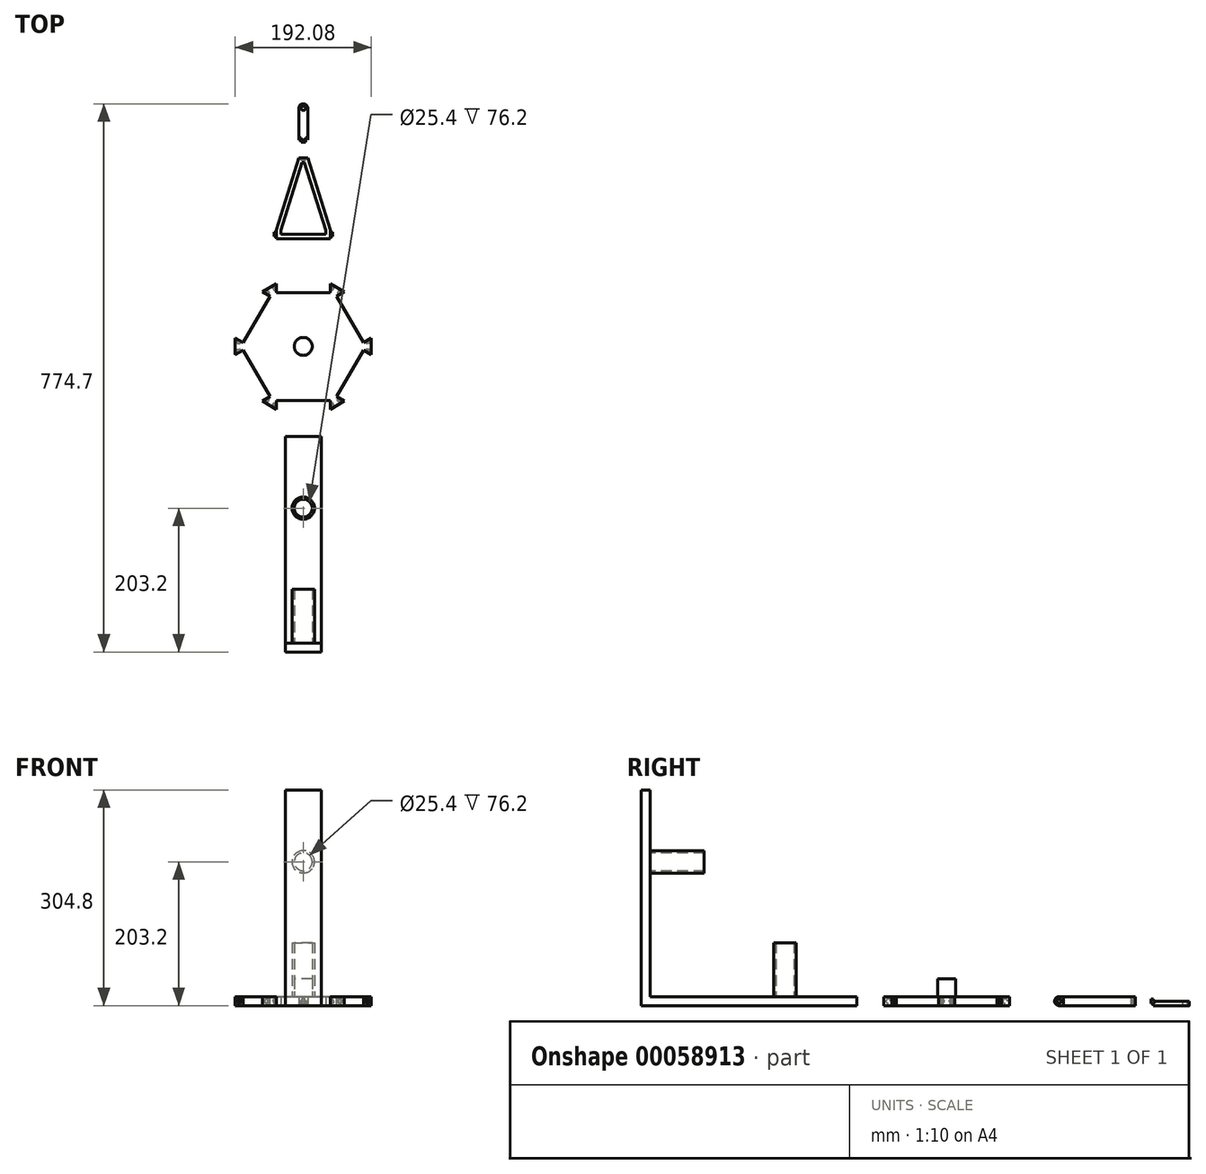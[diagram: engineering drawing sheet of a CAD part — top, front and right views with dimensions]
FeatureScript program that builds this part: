
annotation { "Feature Type Name" : "Feature", "Feature Type Description" : "" }
export const myFeature = defineFeature(function(context is Context, id is Id, definition is map)
    precondition{}
    {
        {
            var Q0;
            Q0=qCreatedBy(makeId("Top.planeOp"),FACE);
            var sketch = newSketch(context, id + "F0", { "sketchPlane" : qUnion([Q0])});
            skCircle(sketch, "E0.cCircle", {"center": v(0, 0) * mm, "radius": 76.2 * mm, "construction": true});
            skLineSegment(sketch, "E0.0", {"start": v(-44, 76.2) * mm, "end": v(44, 76.2) * mm});
            skLineSegment(sketch, "E0.1", {"start": v(44, 76.2) * mm, "end": v(87.99, 0) * mm});
            skLineSegment(sketch, "E0.2", {"start": v(87.99, 0) * mm, "end": v(44, -76.2) * mm});
            skLineSegment(sketch, "E0.3", {"start": v(44, -76.2) * mm, "end": v(-44, -76.2) * mm});
            skLineSegment(sketch, "E0.4", {"start": v(-44, -76.2) * mm, "end": v(-87.99, 0) * mm});
            skLineSegment(sketch, "E0.5", {"start": v(-87.99, 0) * mm, "end": v(-44, 76.2) * mm});
            skPoint(sketch, "E0.0.midPoint", {"position": v(0, 76.2) * mm});
            skSolve(sketch);
        }
        {
            var Q0;
            Q0=makeQuery(id+"F0.imprint","IMPRINT",FACE,{"disambiguationData":[TD([[makeQuery(id+"F0.imprint","IMPRINT",EDGE,{"derivedFrom":sQuery(id+"F0.wireOp",EDGE,"E0.0")}),-1.0]])]});
            extrude(context, id + "F1", {"entities" : qUnion([Q0]), "depth" : 12.7 * mm});
        }
        {
            var Q0;
            Q0=makeQuery(id+"F1.opExtrude","CAP_FACE",FACE,{"disambiguationData":[OSD([sQuery(id+"F0.wireOp",EDGE,"E0.0"),sQuery(id+"F0.wireOp",EDGE,"E0.1"),sQuery(id+"F0.wireOp",EDGE,"E0.2"),sQuery(id+"F0.wireOp",EDGE,"E0.3"),sQuery(id+"F0.wireOp",EDGE,"E0.4"),sQuery(id+"F0.wireOp",EDGE,"E0.5")])],"isStart":false});
            var sketch = newSketch(context, id + "F2", { "sketchPlane" : qUnion([Q0])});
            skLineSegment(sketch, "E1", {"start": v(-85.04, 5.1) * mm, "end": v(-96.04, 11.45) * mm});
            skLineSegment(sketch, "E2", {"start": v(-96.04, 11.45) * mm, "end": v(-96.04, -11.45) * mm});
            skLineSegment(sketch, "E3", {"start": v(-96.04, -11.45) * mm, "end": v(-85.04, -5.1) * mm});
            skLineSegment(sketch, "E4", {"start": v(-120.82, 0) * mm, "end": v(103.85, 0) * mm, "construction": true});
            skLineSegment(sketch, "E5", {"start": v(-85.04, 5.1) * mm, "end": v(-85.04, -5.1) * mm});
            skLineSegment(sketch, "E6", {"start": v(0, 0) * mm, "end": v(-66, 38.1) * mm, "construction": true});
            skSolve(sketch);
        }
        {
            var Q0;
            {var subQ5=sQuery(id+"F2.wireOp",EDGE,"E1");Q0=makeQuery(id+"F2.imprint","IMPRINT",FACE,{"disambiguationData":[TD([[makeQuery(id+"F2.imprint","IMPRINT",EDGE,{"derivedFrom":subQ5}),1.0]])]});}
            var Q1;
            Q1=makeQuery(id+"F1.opExtrude","CAP_FACE",FACE,{"disambiguationData":[OSD([sQuery(id+"F0.wireOp",EDGE,"E0.0"),sQuery(id+"F0.wireOp",EDGE,"E0.1"),sQuery(id+"F0.wireOp",EDGE,"E0.2"),sQuery(id+"F0.wireOp",EDGE,"E0.3"),sQuery(id+"F0.wireOp",EDGE,"E0.4"),sQuery(id+"F0.wireOp",EDGE,"E0.5")])],"isStart":true});
            extrude(context, id + "F3", {"entities" : qUnion([Q0]), "operationType" : NewBodyOperationType.ADD, "endBound" : BoundingType.UP_TO_SURFACE, "oppositeDirection" : true, "endBoundEntityFace" : qUnion([Q1]), "depth" : 25.4 * mm});
        }
        {
            var Q0;
            Q0=makeQuery(id+"F3.opExtrude","SWEPT_FACE",FACE,{"disambiguationData":[OSD([sQuery(id+"F2.wireOp",EDGE,"E3")])]});
            var sketch = newSketch(context, id + "F4", { "sketchPlane" : qUnion([Q0])});
            skPoint(sketch, "E7", {"position": v(-82.55, 6.35) * mm});
            skLineSegment(sketch, "E8", {"start": v(-88.9, 12.7) * mm, "end": v(-76.2, 0) * mm});
            skSolve(sketch);
        }
        {
            var Q0;
            Q0=sQuery(id+"F4.wireOp",VERTEX,"E7");
            var Q1;
            Q1=makeQuery(id+"F1.opExtrude","SWEPT_BODY",BODY,{"disambiguationData":[OSD([sQuery(id+"F0.wireOp",EDGE,"E0.0"),sQuery(id+"F0.wireOp",EDGE,"E0.1"),sQuery(id+"F0.wireOp",EDGE,"E0.2"),sQuery(id+"F0.wireOp",EDGE,"E0.3"),sQuery(id+"F0.wireOp",EDGE,"E0.4"),sQuery(id+"F0.wireOp",EDGE,"E0.5")])]});
            hole(context, id + "F5", {"style" : HoleStyle.SIMPLE, "holeDiameter" : 6.35 * mm, "endStyle" : HoleEndStyle.BLIND, "holeDepth" : 3.17 * mm, "locations" : qUnion([Q0]), "scope" : qUnion([Q1])});
        }
        {
            var Q0;
            Q0=makeQuery(id+"F3.opExtrude","SWEPT_FACE",FACE,{"disambiguationData":[OSD([sQuery(id+"F2.wireOp",EDGE,"E1")])]});
            var sketch = newSketch(context, id + "F6", { "sketchPlane" : qUnion([Q0])});
            skLineSegment(sketch, "E9", {"start": v(76.2, 12.7) * mm, "end": v(88.9, 0) * mm, "construction": true});
            skPoint(sketch, "E10", {"position": v(82.55, 6.35) * mm});
            skSolve(sketch);
        }
        {
            var Q0;
            Q0=sQuery(id+"F6.wireOp",VERTEX,"E10");
            var Q1;
            Q1=makeQuery(id+"F1.opExtrude","SWEPT_BODY",BODY,{"disambiguationData":[OSD([sQuery(id+"F0.wireOp",EDGE,"E0.0"),sQuery(id+"F0.wireOp",EDGE,"E0.1"),sQuery(id+"F0.wireOp",EDGE,"E0.2"),sQuery(id+"F0.wireOp",EDGE,"E0.3"),sQuery(id+"F0.wireOp",EDGE,"E0.4"),sQuery(id+"F0.wireOp",EDGE,"E0.5")])]});
            hole(context, id + "F7", {"style" : HoleStyle.SIMPLE, "holeDiameter" : 6.35 * mm, "endStyle" : HoleEndStyle.BLIND, "holeDepth" : 3.17 * mm, "locations" : qUnion([Q0]), "scope" : qUnion([Q1])});
        }
        {
            var Q0;
            {var subQ0=sQuery(id+"F0.wireOp",EDGE,"E0.5");var subQ1=sQuery(id+"F0.wireOp",EDGE,"E0.4");Q0=makeQuery(id+"F3.boolean.opBoolean","MERGE",FACE,{"derivedFrom":[makeQuery(id+"F1.opExtrude","CAP_FACE",FACE,{"disambiguationData":[OSD([sQuery(id+"F0.wireOp",EDGE,"E0.0"),sQuery(id+"F0.wireOp",EDGE,"E0.1"),sQuery(id+"F0.wireOp",EDGE,"E0.2"),sQuery(id+"F0.wireOp",EDGE,"E0.3"),subQ1,subQ0])],"isStart":false}),makeQuery(id+"F3.opExtrude","CAP_FACE",FACE,{"disambiguationData":[OSD([subQ1,subQ0,sQuery(id+"F2.wireOp",EDGE,"E1"),sQuery(id+"F2.wireOp",EDGE,"E2"),sQuery(id+"F2.wireOp",EDGE,"E3")])],"isStart":true})]});}
            var sketch = newSketch(context, id + "F8", { "sketchPlane" : qUnion([Q0])});
            skCircle(sketch, "E11", {"center": v(0, 0) * mm, "radius": 12.7 * mm});
            skSolve(sketch);
        }
        {
            var Q0;
            Q0 = qSketchRegion(id + "F8", true);
            extrude(context, id + "F9", {"entities" : qUnion([Q0]), "operationType" : NewBodyOperationType.ADD, "depth" : 25.4 * mm});
        }
        {
            var Q0;
            Q0=makeQuery(id+"F1.opExtrude","SWEPT_BODY",BODY,{"disambiguationData":[OSD([sQuery(id+"F0.wireOp",EDGE,"E0.0"),sQuery(id+"F0.wireOp",EDGE,"E0.1"),sQuery(id+"F0.wireOp",EDGE,"E0.2"),sQuery(id+"F0.wireOp",EDGE,"E0.3"),sQuery(id+"F0.wireOp",EDGE,"E0.4"),sQuery(id+"F0.wireOp",EDGE,"E0.5")])]});
            var Q1;
            Q1=makeQuery(id+"F9.opExtrude","SWEPT_FACE",FACE,{"disambiguationData":[OSD([sQuery(id+"F8.wireOp",EDGE,"E11")])]});
            circularPattern(context, id + "F10", {"operationType" : NewBodyOperationType.ADD, "entities" : qUnion([Q0]), "axis" : qUnion([Q1]), "angle" : 60 * degree, "instanceCount" : 6});
        }
        {
            var Q0;
            Q0=qCreatedBy(makeId("Top.planeOp"),FACE);
            var sketch = newSketch(context, id + "F11", { "sketchPlane" : qUnion([Q0])});
            skLineSegment(sketch, "E12", {"start": v(-38.1, 152.4) * mm, "end": v(38.1, 152.4) * mm});
            skLineSegment(sketch, "E13", {"start": v(38.1, 152.4) * mm, "end": v(38.1, 165.1) * mm});
            skLineSegment(sketch, "E14", {"start": v(38.1, 165.1) * mm, "end": v(6.35, 266.7) * mm});
            skLineSegment(sketch, "E15", {"start": v(6.35, 266.7) * mm, "end": v(-6.35, 266.7) * mm});
            skLineSegment(sketch, "E16", {"start": v(-6.35, 266.7) * mm, "end": v(-38.1, 165.1) * mm});
            skLineSegment(sketch, "E17", {"start": v(-38.1, 165.1) * mm, "end": v(-38.1, 152.4) * mm});
            skLineSegment(sketch, "E18", {"start": v(0, 266.7) * mm, "end": v(0, 152.4) * mm, "construction": true});
            skLineSegment(sketch, "E19.0", {"start": v(1.68, 260.35) * mm, "end": v(-1.68, 260.35) * mm});
            skLineSegment(sketch, "E19.1", {"start": v(-31.75, 164.13) * mm, "end": v(-31.75, 158.75) * mm});
            skLineSegment(sketch, "E19.2", {"start": v(-31.75, 158.75) * mm, "end": v(31.75, 158.75) * mm});
            skLineSegment(sketch, "E19.3", {"start": v(-1.68, 260.35) * mm, "end": v(-31.75, 164.13) * mm});
            skLineSegment(sketch, "E19.4", {"start": v(31.75, 158.75) * mm, "end": v(31.75, 164.13) * mm});
            skLineSegment(sketch, "E19.5", {"start": v(31.75, 164.13) * mm, "end": v(1.68, 260.35) * mm});
            skSolve(sketch);
        }
        {
            var Q0;
            Q0=makeQuery(id+"F11.imprint","IMPRINT",FACE,{"disambiguationData":[TD([[makeQuery(id+"F11.imprint","IMPRINT",EDGE,{"derivedFrom":sQuery(id+"F11.wireOp",EDGE,"E12")}),1.0]])]});
            extrude(context, id + "F12", {"entities" : qUnion([Q0]), "depth" : 12.7 * mm});
        }
        {
            var Q0;
            Q0=makeQuery(id+"F12.opExtrude","CAP_EDGE",EDGE,{"disambiguationData":[OSD([sQuery(id+"F11.wireOp",EDGE,"E12")])],"isStart":false});
            var Q1;
            Q1=makeQuery(id+"F12.opExtrude","CAP_EDGE",EDGE,{"disambiguationData":[OSD([sQuery(id+"F11.wireOp",EDGE,"E12")])],"isStart":true});
            fillet(context, id + "F13", {"entities" : qUnion([Q0, Q1]), "radius" : 6.35 * mm, "tangentPropagation" : true, "allowEdgeOverflow" : false});
        }
        {
            var Q0;
            Q0=makeQuery(id+"F12.opExtrude","SWEPT_FACE",FACE,{"disambiguationData":[OSD([sQuery(id+"F11.wireOp",EDGE,"E13")])]});
            var sketch = newSketch(context, id + "F14", { "sketchPlane" : qUnion([Q0])});
            skCircle(sketch, "E20", {"center": v(158.75, 6.35) * mm, "radius": 3.18 * mm});
            skSolve(sketch);
        }
        {
            var Q0;
            Q0=makeQuery(id+"F14.imprint","IMPRINT",FACE,{"disambiguationData":[TD([[makeQuery(id+"F14.imprint","IMPRINT",EDGE,{"derivedFrom":sQuery(id+"F14.wireOp",EDGE,"E20")}),1.0]])]});
            extrude(context, id + "F15", {"entities" : qUnion([Q0]), "operationType" : NewBodyOperationType.ADD, "depth" : 3.17 * mm});
        }
        {
            var Q0;
            Q0=makeQuery(id+"F15.opExtrude","SWEPT_FACE",FACE,{"disambiguationData":[OSD([sQuery(id+"F14.wireOp",EDGE,"E20")])]});
            var Q1;
            Q1=makeQuery(id+"F15.opExtrude","CAP_FACE",FACE,{"disambiguationData":[OSD([sQuery(id+"F14.wireOp",EDGE,"E20")])],"isStart":false});
            var Q2;
            Q2=qCreatedBy(makeId("Right.planeOp"),FACE);
            mirror(context, id + "F16", {"faces" : qUnion([Q0, Q1]), "mirrorPlane" : qUnion([Q2]), "patternType" : MirrorType.FACE});
        }
        {
            var Q0;
            Q0=makeQuery(id+"F12.opExtrude","SWEPT_FACE",FACE,{"disambiguationData":[OSD([sQuery(id+"F11.wireOp",EDGE,"E15")])]});
            var sketch = newSketch(context, id + "F17", { "sketchPlane" : qUnion([Q0])});
            skLineSegment(sketch, "E21", {"start": v(-6.35, 12.7) * mm, "end": v(6.35, 0) * mm, "construction": true});
            skPoint(sketch, "E22", {"position": v(0, 6.35) * mm});
            skSolve(sketch);
        }
        {
            var Q0;
            Q0=sQuery(id+"F17.wireOp",VERTEX,"E22");
            var Q1;
            Q1=makeQuery(id+"F12.opExtrude","SWEPT_BODY",BODY,{"disambiguationData":[OSD([sQuery(id+"F11.wireOp",EDGE,"E12"),sQuery(id+"F11.wireOp",EDGE,"E13"),sQuery(id+"F11.wireOp",EDGE,"E14"),sQuery(id+"F11.wireOp",EDGE,"E15"),sQuery(id+"F11.wireOp",EDGE,"E16"),sQuery(id+"F11.wireOp",EDGE,"E17"),sQuery(id+"F11.wireOp",EDGE,"E19.0"),sQuery(id+"F11.wireOp",EDGE,"E19.1"),sQuery(id+"F11.wireOp",EDGE,"E19.2"),sQuery(id+"F11.wireOp",EDGE,"E19.3"),sQuery(id+"F11.wireOp",EDGE,"E19.4"),sQuery(id+"F11.wireOp",EDGE,"E19.5")])]});
            hole(context, id + "F18", {"style" : HoleStyle.SIMPLE, "holeDiameter" : 6.35 * mm, "endStyle" : HoleEndStyle.BLIND, "holeDepth" : 3.17 * mm, "locations" : qUnion([Q0]), "scope" : qUnion([Q1])});
        }
        {
            var Q0;
            Q0=qCreatedBy(makeId("Top.planeOp"),FACE);
            var sketch = newSketch(context, id + "F19", { "sketchPlane" : qUnion([Q0])});
            skLineSegment(sketch, "E23.rect.bottom", {"start": v(6.35, 292.1) * mm, "end": v(-6.35, 292.1) * mm});
            skLineSegment(sketch, "E23.rect.top", {"start": v(6.35, 342.9) * mm, "end": v(-6.35, 342.9) * mm});
            skLineSegment(sketch, "E23.rect.left", {"start": v(6.35, 292.1) * mm, "end": v(6.35, 342.9) * mm});
            skLineSegment(sketch, "E23.rect.right", {"start": v(-6.35, 292.1) * mm, "end": v(-6.35, 342.9) * mm});
            skPoint(sketch, "E23.rect.middle", {"position": v(0, 317.5) * mm});
            skCircle(sketch, "E24", {"center": v(0, 336.55) * mm, "radius": 3.18 * mm});
            skSolve(sketch);
        }
        {
            var Q0;
            Q0=makeQuery(id+"F19.imprint","IMPRINT",FACE,{"disambiguationData":[TD([[makeQuery(id+"F19.imprint","IMPRINT",EDGE,{"derivedFrom":sQuery(id+"F19.wireOp",EDGE,"E23.rect.bottom")}),-1.0]])]});
            extrude(context, id + "F20", {"entities" : qUnion([Q0]), "depth" : 6.35 * mm});
        }
        {
            var Q0;
            Q0=makeQuery(id+"F20.opExtrude","SWEPT_EDGE",EDGE,{"disambiguationData":[OSD([sQuery(id+"F19.wireOp",EDGE,"E23.rect.top"),sQuery(id+"F19.wireOp",EDGE,"E23.rect.right")])]});
            var Q1;
            Q1=makeQuery(id+"F20.opExtrude","SWEPT_EDGE",EDGE,{"disambiguationData":[OSD([sQuery(id+"F19.wireOp",EDGE,"E23.rect.top"),sQuery(id+"F19.wireOp",EDGE,"E23.rect.left")])]});
            fillet(context, id + "F21", {"entities" : qUnion([Q0, Q1]), "radius" : 6.35 * mm, "tangentPropagation" : true, "allowEdgeOverflow" : false});
        }
        {
            var Q0;
            Q0=makeQuery(id+"F20.opExtrude","SWEPT_FACE",FACE,{"disambiguationData":[OSD([sQuery(id+"F19.wireOp",EDGE,"E23.rect.bottom")])]});
            var sketch = newSketch(context, id + "F22", { "sketchPlane" : qUnion([Q0])});
            skCircle(sketch, "E25", {"center": v(0, 6.35) * mm, "radius": 3.18 * mm});
            skSolve(sketch);
        }
        {
            var Q0;
            {var subQ0=sQuery(id+"F22.wireOp",EDGE,"E25");var subQ1=makeQuery(id+"F20.opExtrude","CAP_EDGE",EDGE,{"disambiguationData":[OSD([sQuery(id+"F19.wireOp",EDGE,"E23.rect.bottom")])],"isStart":false});var subQ2=makeQuery(id+"F22.imprint","INTERSECT",VERTEX,{"disambiguationData":[OD(0.0)],"derivedFrom":[subQ1,subQ0]});Q0=makeQuery(id+"F22.imprint","IMPRINT",FACE,{"disambiguationData":[TD([[makeQuery(id+"F22.imprint","IMPRINT",EDGE,{"disambiguationData":[TD([[subQ2,1.0]])],"derivedFrom":subQ0}),1.0]])]});}
            var Q1;
            {var subQ0=sQuery(id+"F22.wireOp",EDGE,"E25");var subQ1=makeQuery(id+"F20.opExtrude","CAP_EDGE",EDGE,{"disambiguationData":[OSD([sQuery(id+"F19.wireOp",EDGE,"E23.rect.bottom")])],"isStart":false});var subQ2=makeQuery(id+"F22.imprint","INTERSECT",VERTEX,{"disambiguationData":[OD(0.0)],"derivedFrom":[subQ1,subQ0]});Q1=makeQuery(id+"F22.imprint","IMPRINT",FACE,{"disambiguationData":[TD([[makeQuery(id+"F22.imprint","IMPRINT",EDGE,{"disambiguationData":[TD([[subQ2,-1.0]])],"derivedFrom":subQ0}),1.0]])]});}
            extrude(context, id + "F23", {"entities" : qUnion([Q0, Q1]), "operationType" : NewBodyOperationType.ADD, "depth" : 3.17 * mm});
        }
        {
            var Q0;
            {var subQ0=sQuery(id+"F19.wireOp",EDGE,"E23.rect.bottom");Q0=makeQuery(id+"F23.boolean.opBoolean","SPLIT",EDGE,{"disambiguationData":[topologyDisambiguationEdgeConnected([makeQuery(id+"F20.opExtrude","CAP_FACE",FACE,{"disambiguationData":[OSD([subQ0,sQuery(id+"F19.wireOp",EDGE,"E23.rect.top"),sQuery(id+"F19.wireOp",EDGE,"E23.rect.left"),sQuery(id+"F19.wireOp",EDGE,"E23.rect.right"),sQuery(id+"F19.wireOp",EDGE,"E24")])],"isStart":false}),makeQuery(id+"F23.opExtrude","CAP_FACE",FACE,{"disambiguationData":[OSD([sQuery(id+"F22.wireOp",EDGE,"E25")])],"isStart":true})])],"derivedFrom":makeQuery(id+"F20.opExtrude","CAP_EDGE",EDGE,{"disambiguationData":[OSD([subQ0])],"isStart":false})});}
            chamfer(context, id + "F24", {"entities" : qUnion([Q0]), "width" : 3.17 * mm, "tangentPropagation" : true});
        }
        {
            var Q0;
            Q0=qCreatedBy(makeId("Right.planeOp"),FACE);
            var sketch = newSketch(context, id + "F25", { "sketchPlane" : qUnion([Q0])});
            skLineSegment(sketch, "E26", {"start": v(-127, 0) * mm, "end": v(-127, 12.7) * mm});
            skLineSegment(sketch, "E27", {"start": v(-127, 12.7) * mm, "end": v(-419.1, 12.7) * mm});
            skLineSegment(sketch, "E28", {"start": v(-419.1, 12.7) * mm, "end": v(-419.1, 304.8) * mm});
            skLineSegment(sketch, "E29", {"start": v(-419.1, 304.8) * mm, "end": v(-431.8, 304.8) * mm});
            skLineSegment(sketch, "E30", {"start": v(-431.8, 304.8) * mm, "end": v(-431.8, 0) * mm});
            skLineSegment(sketch, "E31", {"start": v(-431.8, 0) * mm, "end": v(-127, 0) * mm});
            skSolve(sketch);
        }
        {
            var Q0;
            Q0=makeQuery(id+"F25.imprint","IMPRINT",FACE,{"disambiguationData":[TD([[makeQuery(id+"F25.imprint","IMPRINT",EDGE,{"derivedFrom":sQuery(id+"F25.wireOp",EDGE,"E26")}),1.0]])]});
            extrude(context, id + "F26", {"entities" : qUnion([Q0]), "endBound" : BoundingType.SYMMETRIC, "depth" : 50.8 * mm});
        }
        {
            var Q0;
            Q0=makeQuery(id+"F26.opExtrude","SWEPT_FACE",FACE,{"disambiguationData":[OSD([sQuery(id+"F25.wireOp",EDGE,"E28")])]});
            var sketch = newSketch(context, id + "F27", { "sketchPlane" : qUnion([Q0])});
            skCircle(sketch, "E32", {"center": v(0, 203.2) * mm, "radius": 12.7 * mm});
            skCircle(sketch, "E33", {"center": v(0, 203.2) * mm, "radius": 15.88 * mm});
            skSolve(sketch);
        }
        {
            var Q0;
            Q0=makeQuery(id+"F27.imprint","IMPRINT",FACE,{"disambiguationData":[TD([[makeQuery(id+"F27.imprint","IMPRINT",EDGE,{"derivedFrom":sQuery(id+"F27.wireOp",EDGE,"E32")}),-1.0]])]});
            extrude(context, id + "F28", {"entities" : qUnion([Q0]), "operationType" : NewBodyOperationType.ADD, "depth" : 76.2 * mm});
        }
        {
            var Q0;
            Q0=makeQuery(id+"F26.opExtrude","SWEPT_FACE",FACE,{"disambiguationData":[OSD([sQuery(id+"F25.wireOp",EDGE,"E27")])]});
            var sketch = newSketch(context, id + "F29", { "sketchPlane" : qUnion([Q0])});
            skCircle(sketch, "E34", {"center": v(0, -228.6) * mm, "radius": 15.88 * mm});
            skCircle(sketch, "E35", {"center": v(0, -228.6) * mm, "radius": 12.7 * mm});
            skSolve(sketch);
        }
        {
            var Q0;
            Q0=makeQuery(id+"F29.imprint","IMPRINT",FACE,{"disambiguationData":[TD([[makeQuery(id+"F29.imprint","IMPRINT",EDGE,{"derivedFrom":sQuery(id+"F29.wireOp",EDGE,"E34")}),1.0]])]});
            extrude(context, id + "F30", {"entities" : qUnion([Q0]), "operationType" : NewBodyOperationType.ADD, "depth" : 76.2 * mm});
        }
    });
